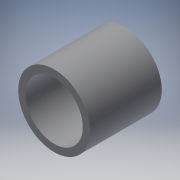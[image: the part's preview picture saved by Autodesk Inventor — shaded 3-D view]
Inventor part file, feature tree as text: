
AUTODESK INVENTOR PART (.ipt)
format: ipt  version: 2018.2 (Build 222227000, 227)  size: 99,328 bytes
history: native  units: mm
features: other x1, extrude x1, sketch x1
ambient origin geometry x8: Origin, YZ Plane, XZ Plane, XY Plane, X Axis, Y Axis, Z Axis, Center Point
bodies: Body1 (feature_tree)
feature tree (3):
  other  "ソリッド1"
  extrude  "押し出し1"  Depth=10.0mm
  sketch  "スケッチ1"
